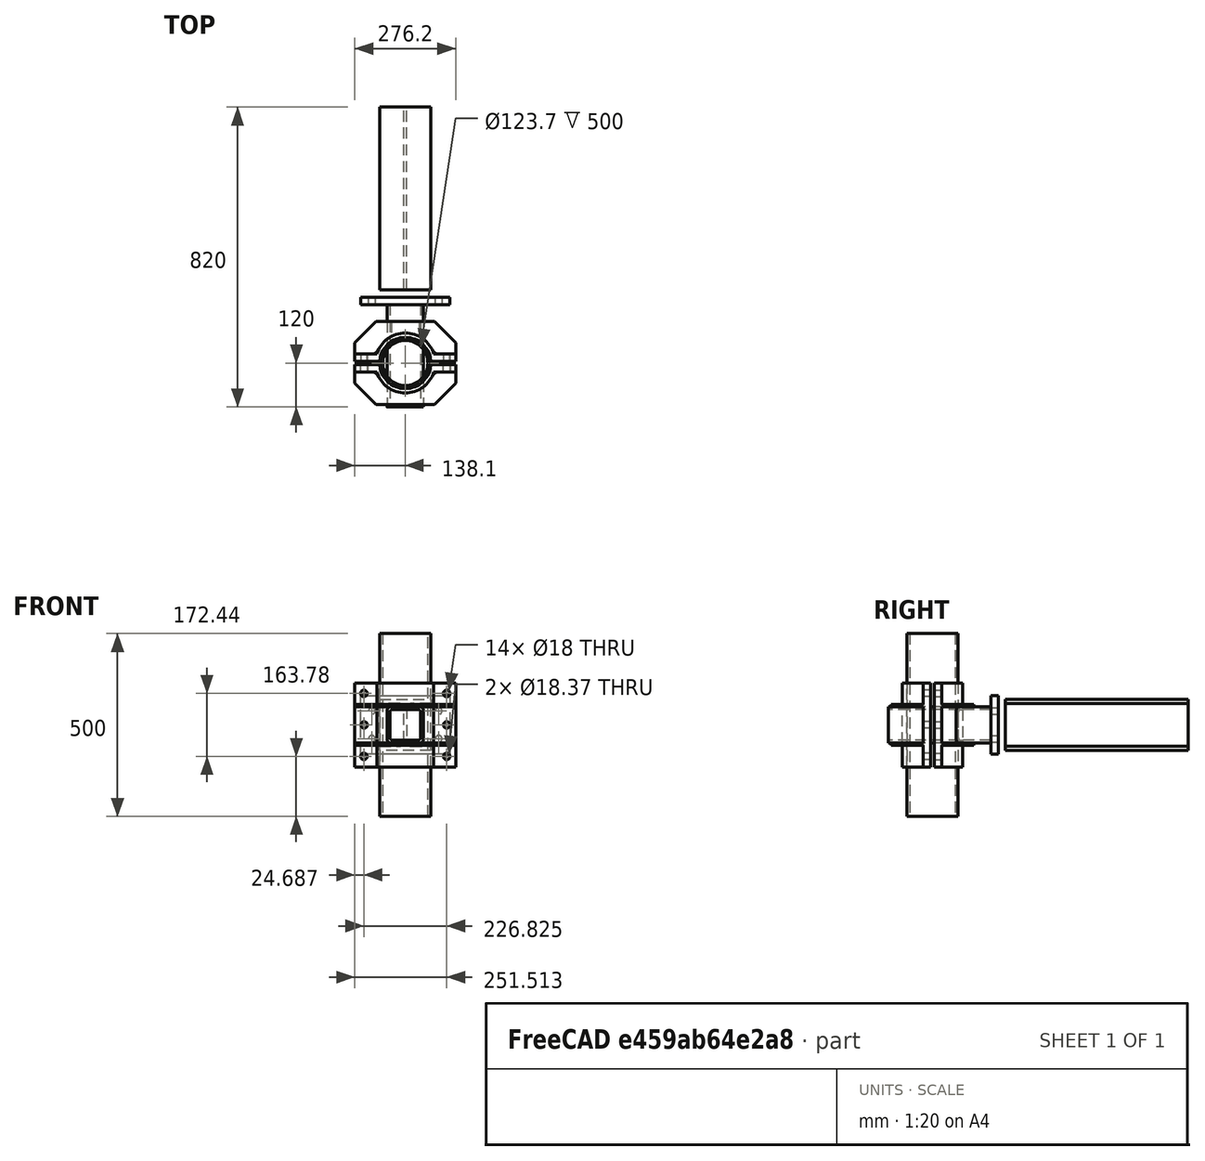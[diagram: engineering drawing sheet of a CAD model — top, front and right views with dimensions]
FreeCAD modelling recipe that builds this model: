
FCSTD DOCUMENT  (FreeCAD 0.21R33694 (Git))
Label: Schelle_fem
License: All rights reserved
LicenseURL: http://en.wikipedia.org/wiki/All_rights_reserved
objects: Part::FeaturePython×7, Sketcher::SketchObject×5, Part::Extrusion×4, Part::Feature×3, Part::MultiFuse×2, Fem::ConstraintForce×2, App::DocumentObjectGroup×1, Part::Cut×1, Fem::FemSolverObjectPython×1, App::MaterialObjectPython×1, Fem::ConstraintFixed×1, Fem::FeaturePython×1, Fem::FemMeshObjectPython×1, Fem::FemAnalysis×1
note: 22 computed .brp shape members not serialized (recipe doc carries the construction recipe); baked Part::Feature solids carry a one-line shape summary decoded from their .brp

FEATURE [Part::Feature] BOLTS_part  label="HEB140, l=500.0"
  Placement = pos=(0,0,0) rot=(-1,0,0;1.5708rad)
  shape: bbox 140 x 500 x 140 mm, 18 faces (baked)
FEATURE [Part::Feature] BOLTS_part001  label="Circular hollow profile 139.7/8.0 l=500.0"
  Placement = pos=(0,-200,-250) rot=(0,0,1;0rad)
  shape: bbox 139.7 x 139.7 x 500 mm, 4 faces (baked)
FEATURE [Part::Feature] BOLTS_part002  label="Square hollow profile 100.0/8.0 l=300.0"
  Placement = pos=(0,-20,0) rot=(1,0,0;1.5708rad)
  shape: bbox 100 x 300 x 100 mm, 18 faces (baked)
FEATURE [Sketcher::SketchObject] Sketch
  FullyConstrained = false
  Placement = pos=(0,0,0) rot=(1,0,0;1.5708rad)
  sketch-geometry (12):
    g0: LineSegment StartX=-121.553 StartY=80 StartZ=0 EndX=121.553 EndY=80 EndZ=0
    g1: LineSegment StartX=121.553 StartY=80 StartZ=0 EndX=121.553 EndY=-80 EndZ=0
    g2: LineSegment StartX=121.553 StartY=-80 StartZ=0 EndX=-121.553 EndY=-80 EndZ=0
    g3: LineSegment StartX=-121.553 StartY=-80 StartZ=0 EndX=-121.553 EndY=80 EndZ=0
    g4: LineSegment StartX=-91.5043 StartY=38.0478 StartZ=0 EndX=91.5043 EndY=38.0478 EndZ=0
    g5: LineSegment StartX=91.5043 StartY=38.0478 StartZ=0 EndX=91.5043 EndY=-38.0478 EndZ=0
    g6: LineSegment StartX=91.5043 StartY=-38.0478 StartZ=0 EndX=-91.5043 EndY=-38.0478 EndZ=0
    g7: LineSegment StartX=-91.5043 StartY=-38.0478 StartZ=0 EndX=-91.5043 EndY=38.0478 EndZ=0
    g8: Circle CenterX=91.5043 CenterY=38.0478 CenterZ=0 NormalX=0 NormalY=0 NormalZ=1 AngleXU=0 Radius=9
    g9: Circle CenterX=91.5043 CenterY=-38.0478 CenterZ=0 NormalX=0 NormalY=0 NormalZ=1 AngleXU=0 Radius=9
    g10: Circle CenterX=-91.5043 CenterY=38.0478 CenterZ=0 NormalX=0 NormalY=0 NormalZ=1 AngleXU=0 Radius=9
    g11: Circle CenterX=-91.5043 CenterY=-38.0478 CenterZ=0 NormalX=0 NormalY=0 NormalZ=1 AngleXU=0 Radius=9
  constraints (25):
    c: Coincident(g0,g1)
    c: Coincident(g1,g2)
    c: Coincident(g2,g3)
    c: Coincident(g3,g0)
    c: Horizontal(g0)
    c: Vertical(g3)
    c: Symmetric(g1,g0,g-1)
    c: Symmetric(g2,g1,g-2)
    c: DistanceY(g1,g1) = 160
    c: Coincident(g4,g5)
    c: Coincident(g5,g6)
    c: Coincident(g6,g7)
    c: Coincident(g7,g4)
    c: Horizontal(g4)
    c: Vertical(g7)
    c: Symmetric(g5,g4,g-1)
    c: Symmetric(g6,g5,g-2)
    c: Coincident(g8,g4)
    c: Coincident(g9,g5)
    c: Coincident(g10,g4)
    c: Coincident(g11,g6)
    c: Equal(g9,g8)
    c: Equal(g9,g10)
    c: Equal(g9,g11)
    c: Diameter(g9) = 18
FEATURE [Part::Extrusion] Extrude  label="flansch"
  Base = -> Sketch
  Dir = (0,-1,0)
  DirMode = 0
  FaceMakerClass = Part::FaceMakerBullseye
  LengthFwd = 20
  LengthRev = 0
  Solid = true
  Symmetric = false
FEATURE [Sketcher::SketchObject] Sketch001
  ExternalGeometry = -> [BOLTS_part001]
  FullyConstrained = true
  sketch-geometry (10):
    g0: ArcOfCircle CenterX=0 CenterY=-200 CenterZ=0 NormalX=0 NormalY=0 NormalZ=1 AngleXU=0 Radius=82 StartAngle=0.30981 EndAngle=2.83178
    g1: ArcOfCircle CenterX=0 CenterY=-200 CenterZ=0 NormalX=0 NormalY=0 NormalZ=1 AngleXU=0 Radius=70 StartAngle=0.0714894 EndAngle=3.0701
    g2: LineSegment StartX=-78.0961 StartY=-175 StartZ=0 EndX=-138.096 EndY=-175 EndZ=0
    g3: LineSegment StartX=-138.096 StartY=-175 StartZ=0 EndX=-138.096 EndY=-195 EndZ=0
    g4: LineSegment StartX=-138.096 StartY=-195 StartZ=0 EndX=-69.8212 EndY=-195 EndZ=0
    g5: LineSegment StartX=-78.0961 StartY=-175 StartZ=0 EndX=-66.6674 EndY=-178.659 EndZ=0
    g6: LineSegment StartX=0 StartY=-200 StartZ=0 EndX=-138.096 EndY=-200 EndZ=0
    g7: LineSegment StartX=69.8212 StartY=-195 StartZ=0 EndX=138.096 EndY=-195 EndZ=0
    g8: LineSegment StartX=138.096 StartY=-195 StartZ=0 EndX=138.096 EndY=-175 EndZ=0
    g9: LineSegment StartX=138.096 StartY=-175 StartZ=0 EndX=78.0961 EndY=-175 EndZ=0
  constraints (30):
    c: Coincident(g0,g-3)
    c: Coincident(g1,g0)
    c: Diameter(g1) = 140
    c: Coincident(g0,g2)
    c: Horizontal(g2)
    c: Coincident(g2,g3)
    c: Coincident(g3,g4)
    c: Horizontal(g4)
    c: Vertical(g3)
    c: Coincident(g4,g1)
    c: DistanceY(g3,g3) = 20
    c: Coincident(g5,g0)
    c: PointOnObject(g5,g1)
    c: Perpendicular(g1,g5)
    c: Distance(g5) = 12
    c: Coincident(g6,g0)
    c: Horizontal(g6)
    c: Vertical(g6,g3)
    c: DistanceY(g6,g3) = 5
    c: DistanceX(g2,g2) = 60
    c: Coincident(g1,g7)
    c: Horizontal(g7)
    c: Coincident(g7,g8)
    c: Vertical(g8)
    c: Coincident(g8,g9)
    c: Horizontal(g9)
    c: Horizontal(g1,g1)
    c: Equal(g2,g9)
    c: Equal(g3,g8)
    c: Coincident(g0,g9)
FEATURE [Part::Extrusion] Extrude001  label="schellenblech"
  Base = -> Sketch001
  Dir = (0,0,1)
  DirMode = 0
  FaceMakerClass = Part::FaceMakerBullseye
  LengthFwd = 230
  LengthRev = 0
  Solid = true
  Symmetric = true
FEATURE [Part::FeaturePython] Clone  label="flansch001"  # Draft clone (typed FeaturePython)
  AttacherType = Attacher::AttachEngine3D
  Fuse = false
  Objects = -> [Extrude]
  Placement = pos=(0,-20,0) rot=(0,0,1;0rad)
  Scale = (1,1,1)
FEATURE [Part::FeaturePython] Facebinder  # WARN: FeaturePython — macro-defined, semantics opaque (R4)
  Area = 47564.4
  Extrusion = 0
  Faces = -> [Extrude001]
  RemoveSplitter = false
  Sew = false
FEATURE [Part::FeaturePython] Slice  # WARN: FeaturePython — macro-defined, semantics opaque (R4)
  Base = -> BOLTS_part002
  Mode = 1
  Tolerance = 0
  Tools = -> [Facebinder]
FEATURE [Part::FeaturePython] Slice_child0  label="Slice.0"  # WARN: FeaturePython — macro-defined, semantics opaque (R4)
  Base = -> Slice
  FilterType = 1
  Invert = false
  OverrideMaxVal = 0
  WindowFrom = 80
  WindowTo = 100
  items = 0
FEATURE [Part::FeaturePython] Slice_child1  label="Slice.1"  # WARN: FeaturePython — macro-defined, semantics opaque (R4)
  Base = -> Slice
  FilterType = 1
  Invert = false
  OverrideMaxVal = 0
  WindowFrom = 80
  WindowTo = 100
  items = 1
FEATURE [App::DocumentObjectGroup] GrExplode_Slice  label="Exploded Slice"
  Group = -> [Slice_child1]
FEATURE [Sketcher::SketchObject] Sketch002
  ExternalGeometry = -> [Extrude001,BOLTS_part001]
  FullyConstrained = true
  sketch-geometry (10):
    g0: LineSegment StartX=-138.096 StartY=-175 StartZ=0 EndX=-138.096 EndY=-145 EndZ=0
    g1: LineSegment StartX=-138.096 StartY=-145 StartZ=0 EndX=-80 EndY=-86.9039 EndZ=0
    g2: LineSegment StartX=-80 StartY=-86.9039 StartZ=0 EndX=80 EndY=-86.9039 EndZ=0
    g3: LineSegment StartX=80 StartY=-86.9039 StartZ=0 EndX=138.096 EndY=-145 EndZ=0
    g4: LineSegment StartX=138.096 StartY=-145 StartZ=0 EndX=138.096 EndY=-175 EndZ=0
    g5: LineSegment StartX=138.096 StartY=-175 StartZ=0 EndX=86.0961 EndY=-175 EndZ=0
    g6: LineSegment StartX=-138.096 StartY=-175 StartZ=0 EndX=-86.0961 EndY=-175 EndZ=0
    g7: LineSegment StartX=-86.0961 StartY=-175 StartZ=0 EndX=-74.3449 EndY=-167.222 EndZ=0
    g8: LineSegment StartX=86.0961 StartY=-175 StartZ=0 EndX=74.3449 EndY=-167.222 EndZ=0
    g9: ArcOfCircle CenterX=0 CenterY=-200 CenterZ=0 NormalX=0 NormalY=0 NormalZ=1 AngleXU=0 Radius=81.25 StartAngle=0.415252 EndAngle=2.72634
  constraints (27):
    c: Coincident(g-4,g0)
    c: Vertical(g0)
    c: Coincident(g0,g1)
    c: Coincident(g1,g2)
    c: Coincident(g2,g3)
    c: Coincident(g3,g4)
    c: Coincident(g4,g-3)
    c: Vertical(g4)
    c: Coincident(g4,g5)
    c: Horizontal(g5)
    c: Coincident(g6,g0)
    c: Horizontal(g6)
    c: Equal(g0,g4)
    c: DistanceY(g4,g4) = 30
    c: Symmetric(g1,g2,g-2)
    c: Angle(g0,g1) = 2.35619
    c: DistanceX(g2,g2) = 160
    c: Coincident(g7,g6)
    c: Coincident(g8,g5)
    c: Coincident(g9,g-5)
    c: Coincident(g9,g7)
    c: Coincident(g9,g8)
    c: Diameter(g9) = 162.5
    c: Equal(g6,g5)
    c: DistanceX(g6,g6) = 52
    c: Equal(g7,g8)
    c: Angle(g5,g8) = 2.55691
FEATURE [Part::Extrusion] Extrude002
  Base = -> Sketch002
  Dir = (0,0,1)
  DirMode = 0
  FaceMakerClass = Part::FaceMakerBullseye
  LengthFwd = 6
  LengthRev = 0
  Placement = pos=(0,0,50) rot=(0,0,1;0rad)
  Solid = true
  Symmetric = false
FEATURE [Part::FeaturePython] Clone001  label="Extrude003"  # Draft clone (typed FeaturePython)
  AttacherType = Attacher::AttachEngine3D
  Fuse = false
  Objects = -> [Extrude002]
  Placement = pos=(0,0,-56) rot=(0,0,1;0rad)
  Scale = (1,1,1)
FEATURE [Sketcher::SketchObject] Sketch003
  ExternalGeometry = -> [Extrude001]
  FullyConstrained = false
  MapMode = 5
  Placement = pos=(0,-175,0) rot=(0,0.707107,0.707107;3.14159rad)
  Support = -> [Extrude001]
  sketch-geometry (17):
    g0: Circle CenterX=-113.413 CenterY=86.22 CenterZ=0 NormalX=0 NormalY=0 NormalZ=1 AngleXU=0 Radius=9
    g1: Circle CenterX=-113.413 CenterY=-86.22 CenterZ=0 NormalX=0 NormalY=0 NormalZ=1 AngleXU=0 Radius=9.18475
    g2: Circle CenterX=113.413 CenterY=-86.22 CenterZ=0 NormalX=0 NormalY=0 NormalZ=1 AngleXU=0 Radius=9
    g3: Circle CenterX=113.413 CenterY=86.22 CenterZ=0 NormalX=0 NormalY=0 NormalZ=1 AngleXU=0 Radius=9
    g4: Circle CenterX=112.569 CenterY=0 CenterZ=0 NormalX=0 NormalY=0 NormalZ=1 AngleXU=0 Radius=9
    g5: Circle CenterX=-113.413 CenterY=0 CenterZ=0 NormalX=0 NormalY=0 NormalZ=1 AngleXU=0 Radius=9
    g6: LineSegment StartX=-113.413 StartY=86.22 StartZ=0 EndX=-113.413 EndY=-86.22 EndZ=0
    g7: LineSegment StartX=113.413 StartY=86.22 StartZ=0 EndX=113.413 EndY=-86.22 EndZ=0
    g8: LineSegment StartX=-113.413 StartY=86.22 StartZ=0 EndX=113.413 EndY=86.22 EndZ=0
    g9: LineSegment StartX=-113.413 StartY=-86.22 StartZ=0 EndX=113.413 EndY=-86.22 EndZ=0
    g10: LineSegment StartX=-113.413 StartY=86.22 StartZ=0 EndX=-142.096 EndY=106.277 EndZ=0
    g11: LineSegment StartX=-113.413 StartY=-86.22 StartZ=0 EndX=-138.096 EndY=-115 EndZ=0
    g12: LineSegment StartX=113.413 StartY=-86.22 StartZ=0 EndX=138.096 EndY=-115 EndZ=0
    g13: LineSegment StartX=113.413 StartY=86.22 StartZ=0 EndX=133.33 EndY=115 EndZ=0
    g14: LineSegment StartX=-113.413 StartY=86.22 StartZ=0 EndX=-113.413 EndY=115 EndZ=0
    g15: LineSegment StartX=113.413 StartY=86.22 StartZ=0 EndX=113.413 EndY=115 EndZ=0
    g16: LineSegment StartX=113.413 StartY=-86.22 StartZ=0 EndX=113.413 EndY=-115 EndZ=0
  constraints (39):
    c: Equal(g0,g5)
    c: Equal(g0,g2)
    c: Equal(g0,g4)
    c: Equal(g0,g3)
    c: Diameter(g0) = 18
    c: Coincident(g6,g0)
    c: Coincident(g6,g1)
    c: Vertical(g6)
    c: Coincident(g7,g3)
    c: Coincident(g7,g2)
    c: Vertical(g7)
    c: Coincident(g8,g0)
    c: Coincident(g8,g3)
    c: Horizontal(g8)
    c: Coincident(g9,g1)
    c: Coincident(g9,g2)
    c: Horizontal(g9)
    c: Coincident(g10,g0)
    c: Coincident(g11,g1)
    c: Coincident(g11,g-4)
    c: Coincident(g12,g2)
    c: Coincident(g12,g-6)
    c: Coincident(g13,g3)
    c: PointOnObject(g13,g-5)
    c: Equal(g10,g13)
    c: Equal(g11,g12)
    c: Distance(g10) = 35
    c: Coincident(g14,g0)
    c: PointOnObject(g14,g-3)
    c: Vertical(g14)
    c: Coincident(g15,g3)
    c: PointOnObject(g15,g-5)
    c: Vertical(g15)
    c: Coincident(g16,g2)
    c: PointOnObject(g16,g-6)
    c: Vertical(g16)
    c: Symmetric(g6,g6,g5)
    c: Horizontal(g5,g-1)
    c: Horizontal(g-1,g4)
FEATURE [Part::Extrusion] Extrude003  label="Loch"
  Base = -> Sketch003
  Dir = (0,-1,0)
  DirMode = 0
  FaceMakerClass = Part::FaceMakerBullseye
  LengthFwd = 60
  LengthRev = 0
  Solid = true
  Symmetric = true
FEATURE [Part::Cut] Cut
  Base = -> Extrude001
  Tool = -> Extrude003
FEATURE [Part::MultiFuse] Fusion  label="Schelle"
  Shapes = -> [Clone001,Extrude002,Cut]
FEATURE [Part::FeaturePython] Clone002  label="Schelle001"  # Draft clone (typed FeaturePython)
  AttacherType = Attacher::AttachEngine3D
  Fuse = false
  Objects = -> [Fusion]
  Placement = pos=(0,-400,0) rot=(1,0,0;3.14159rad)
  Scale = (1,1,1)
FEATURE [Sketcher::SketchObject] Sketch004
  FullyConstrained = false
  MapMode = 5
  Placement = pos=(0,500,0) rot=(-1,0,0;1.5708rad)
  Support = -> [BOLTS_part]
  sketch-geometry (14):
    g0: LineSegment StartX=0.135599 StartY=-0.0219419 StartZ=0 EndX=0.433662 EndY=0.305485 EndZ=0
    g1: LineSegment StartX=0.433662 StartY=0.305485 StartZ=0 EndX=0.299133 EndY=0.727328 EndZ=0
    g2: LineSegment StartX=0.299133 StartY=0.727328 StartZ=0 EndX=-0.133458 EndY=0.821744 EndZ=0
    g3: LineSegment StartX=-0.133458 StartY=0.821744 StartZ=0 EndX=-0.431521 EndY=0.494318 EndZ=0
    g4: LineSegment StartX=-0.431521 StartY=0.494318 StartZ=0 EndX=-0.296992 EndY=0.0724743 EndZ=0
    g5: LineSegment StartX=-0.296992 StartY=0.0724743 StartZ=0 EndX=0.135599 EndY=-0.0219419 EndZ=0
    g6: Circle CenterX=0.00107051 CenterY=0.399901 CenterZ=0 NormalX=0 NormalY=0 NormalZ=1 AngleXU=0 Radius=0.442775
    g7: LineSegment StartX=-5.50953 StartY=118.124 StartZ=0 EndX=-104.408 EndY=54.8169 EndZ=0
    g8: LineSegment StartX=-104.408 StartY=54.8169 StartZ=0 EndX=-99.0318 EndY=-62.485 EndZ=0
    g9: LineSegment StartX=-99.0318 StartY=-62.485 StartZ=0 EndX=5.24261 EndY=-116.48 EndZ=0
    g10: LineSegment StartX=5.24261 StartY=-116.48 StartZ=0 EndX=104.141 EndY=-53.1734 EndZ=0
    g11: LineSegment StartX=104.141 StartY=-53.1734 StartZ=0 EndX=98.7649 EndY=64.1285 EndZ=0
    g12: LineSegment StartX=98.7649 StartY=64.1285 StartZ=0 EndX=-5.50953 EndY=118.124 EndZ=0
    g13: Circle CenterX=-0.133458 CenterY=0.821744 CenterZ=0 NormalX=0 NormalY=0 NormalZ=1 AngleXU=0 Radius=117.425
  constraints (27):
    c: Coincident(g0,g1)
    c: Coincident(g1,g2)
    c: Coincident(g2,g3)
    c: Coincident(g3,g4)
    c: Coincident(g4,g5)
    c: Coincident(g5,g0)
    c: Equal(g0, g1-g5) x5
    c: PointOnObject(g0,g6)
    c: PointOnObject(g1,g6)
    c: PointOnObject(g2,g6)
    c: PointOnObject(g3,g6)
    c: PointOnObject(g4,g6)
    c: PointOnObject(g5,g6)
    c: Coincident(g7,g8)
    c: Coincident(g8,g9)
    c: Coincident(g9,g10)
    c: Coincident(g10,g11)
    c: Coincident(g11,g12)
    c: Coincident(g12,g7)
    c: Equal(g7, g8-g12) x5
    c: PointOnObject(g7,g13)
    c: PointOnObject(g8,g13)
    c: PointOnObject(g9,g13)
    c: PointOnObject(g10,g13)
    c: PointOnObject(g11,g13)
    c: PointOnObject(g12,g13)
    c: Coincident(g13,g2)
FEATURE [Fem::FemSolverObjectPython] SolverCcxTools  # FEM object (typed FeaturePython)
  AnalysisType = 0
  BeamShellResultOutput3D = false
  BucklingFactors = 1
  EigenmodeHighLimit = 1000000
  EigenmodeLowLimit = 0
  EigenmodesCount = 10
  GeometricalNonlinearity = 0
  IterationsControlParameterCutb = 0.25,0.5,0.75,0.85,,,1.5,
  IterationsControlParameterIter = 4,8,9,200,10,400,,200,,
  IterationsControlParameterTimeUse = false
  IterationsThermoMechMaximum = 2000
  IterationsUserDefinedIncrementations = false
  IterationsUserDefinedTimeStepLength = false
  MaterialNonlinearity = 0
  MatrixSolverType = 0
  SplitInputWriter = true
  ThermoMechSteadyState = true
  TimeEnd = 1
  TimeInitialStep = 0.01
FEATURE [App::MaterialObjectPython] MaterialSolid  label="S235"  # material (typed FeaturePython)
  Category = 0
  Material = AuthorAndLicense=(c) 2013 Juergen Riegel (CC-BY 3.0),CardName=CalculiX-Steel,Density=7900 kg/m^3,+8 more (map truncated)
FEATURE [Part::MultiFuse] Fusion001  label="KlemmeFEM"
  Refine = true
  Shapes = -> [Fusion,Slice_child0,Clone]
FEATURE [Fem::ConstraintFixed] ConstraintFixed
  NormalDirection = (-1,0,-1e-16)
  Normals = (72) [(1,0,0),(-0.5,-1.90526e-16,-0.866025),(-0.5,1.90526e-16,0.866025),(1,5.38845e-32,2.44929e-16),(1,0,0),(-0.5,-1.90526e-16,-0.866025),+66 more]
  Points = (72) [(104.413,-195,86.22),(117.913,-195,94.0142),(117.913,-195,78.4257),(104.413,-195,86.22),(104.413,-185,86.22),(117.913,-185,94.0142),+66 more]
  References = -> [Fusion001]
  Scale = 5
FEATURE [Fem::ConstraintForce] ConstraintForce001
  Direction = -> Extrude [Edge2]
  DirectionVector = (0,-1,0)
  Force = 47000
  NormalDirection = (0,0,1)
  Points = (12) [(-121.553,-40,80),(-40.5175,-40,80),(40.5175,-40,80),(121.553,-40,80),(-121.553,-30,80),(-40.5175,-30,80),(40.5175,-30,80),(121.553,-30,80),+4 more]
  References = -> [Fusion001]
  Scale = 12
FEATURE [Fem::FeaturePython] MeshRegion  # FEM object (typed FeaturePython)
  CharacteristicLength = 3
  References = -> [Fusion001]
FEATURE [Fem::FemMeshObjectPython] FEMMeshGmsh  # FEM object (typed FeaturePython)
  Algorithm2D = 0
  Algorithm3D = 0
  CharacteristicLengthMax = 10
  CharacteristicLengthMin = 0
  CoherenceMesh = true
  ElementDimension = 3
  ElementOrder = 1
  GeometryTolerance = 1e-06
  GroupsOfNodes = false
  HighOrderOptimize = 0
  MeshRegionList = -> [MeshRegion]
  MeshSizeFromCurvature = 12
  OptimizeNetgen = false
  OptimizeStd = true
  Part = -> Fusion001
  RecombinationAlgorithm = 0
  Recombine3DAll = false
  RecombineAll = false
  SecondOrderLinear = false
FEATURE [Fem::ConstraintForce] ConstraintForce
  Direction = -> Extrude [Edge5]
  DirectionVector = (0,1,0)
  Force = 47000
  NormalDirection = (0,0,-1)
  Points = (12) [(121.553,-40,-80),(40.5175,-40,-80),(-40.5175,-40,-80),(-121.553,-40,-80),(121.553,-30,-80),(40.5175,-30,-80),(-40.5175,-30,-80),(-121.553,-30,-80),+4 more]
  References = -> [Fusion001]
  Reversed = true
  Scale = 12
FEATURE [Fem::FemAnalysis] Analysis
  Group = -> [SolverCcxTools,MaterialSolid,ConstraintFixed,ConstraintForce001,FEMMeshGmsh,ConstraintForce]
